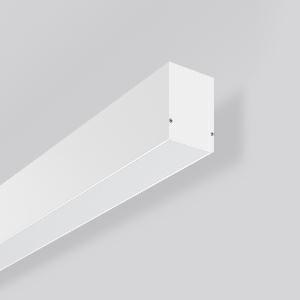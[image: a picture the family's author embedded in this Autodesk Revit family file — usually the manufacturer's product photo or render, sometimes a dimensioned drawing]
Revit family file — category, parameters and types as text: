
# Revit family: less_is_more_50_312605_002_1_bfb3
name_source: partatom
category: Lighting Fixtures
units: mm (PartAtom-declared; Revit-internal decimal feet)

## family parameters
Cut with Voids When Loaded = No
Host = Face
Light Source = No
Part Type = Normal
Room Calculation Point = No
Round Connector Dimension = Use Diameter
Shared = No

## types (1)
- LESS IS MORE 50 (1 x LED Modul 840, 1150 lm, 4000)
    Apparent Load = 9 VA
    CIE Flux Codes = 48 80 96 100 100
    Color Rendering = 80
    Color Temperature = 4000
    Default Elevation = 1800 mm
    Description = Series: LESS IS MORE 50
Linear wall luminaires. Housing: extruded aluminium profile, powder-coated. End cap aluminium powder-coated. Diffuser made of non-yellowing plastic (PMMA), opal. Direct light emission. Suitable for Wall (surface). LED unit with integrated converter interchangeable and removable. Suitable for through-wiring. With sensors or as a safety luminaire on request. 
Colour: traffic white, matt (RAL 9016)
Length: 847 mm
Width: 67 mm
Height: 75 mm
Lamp: LED
Socket: without socket
Colour temperature: 4000K
Colour rendering index (CRI): 80
System power: 9 W
Rated luminous flux: 1150 lm
Luminous efficiency: 128 lm/W
Control gear: Regulated power supply
Protection class: I
Type of protection: IP 20
    Height = 75 mm
    Lamp = 1 x LED Modul 840
    Lamp Light Flux = 1150 lm
    Lamp count = 1
    Length = 847 mm
    Lifetime = 50000 h
    Luminous efficacy = 128 lm/W
    Manufacturer = RZB
    ModVariant = No
    Model = 312605.002.1
    Mounting Place = Wall
    Mounting Type = Surface mounted
    Number of Poles = 1
    OnlyDefault = Yes
    Power Factor = 1
    Product Name = LESS IS MORE 50
    Product group = Surface mounted LED linear luminaires
    ProductGroupID = 2007
    Protection Class = Protection class I
    Protection Degree = IP 20
    RLX_Detail_Level = 1
    RLX_Emergency_Light_Flux = 0 lm
    RLX_Emergency_Type = 0
    RLX_Emergency_Type_DB = No
    RlxData = <blob elided: 35109 chars, md5=4f42103d>
    Socket = socket
    Standby Power = 0 W
    System Light Flux = 1150 lm
    System Power = 9 W
    Type Comments = Product without accessories
    Type Image = 312606.002.jpg
    URL = http://relux.com
    VarID = ---
    Voltage = 0 V
    Weight = 0.00 kg
    Width = 67 mm

## geometry (parser evidence)
native form markers: Blend x4, Sweep x10
no freeform markers — native parametric forms only
